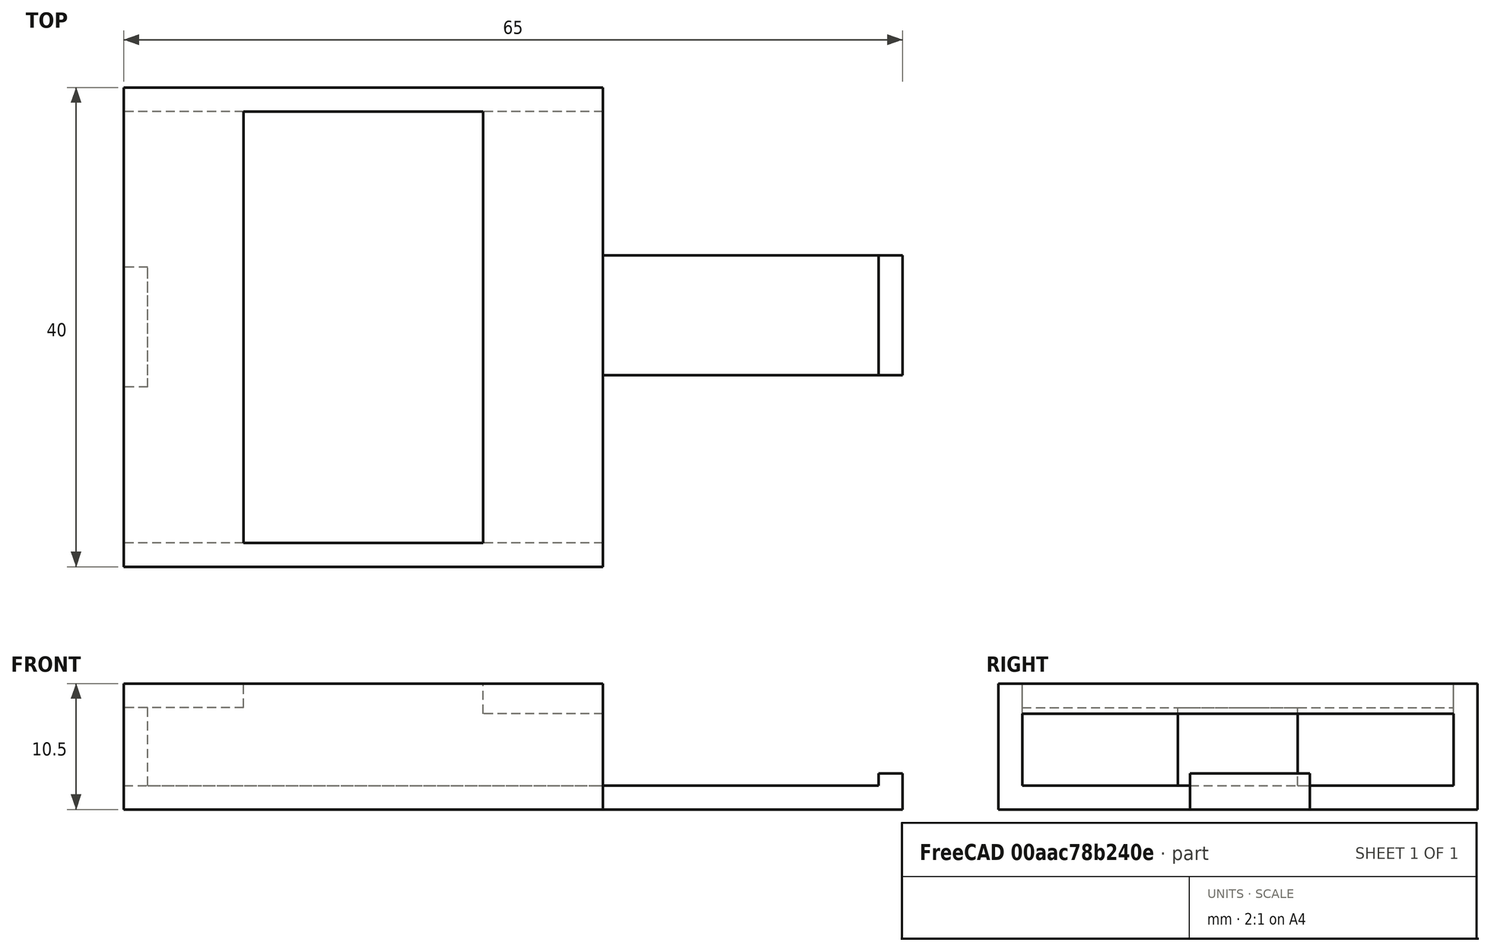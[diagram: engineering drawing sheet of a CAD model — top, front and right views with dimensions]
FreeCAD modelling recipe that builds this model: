
FCSTD DOCUMENT  (FreeCAD 0.20R29603 (Git))
Label: batteryholder
License: All rights reserved
LicenseURL: http://en.wikipedia.org/wiki/All_rights_reserved
objects: Part::Box×8, Part::MultiFuse×1
note: 9 computed .brp shape members not serialized (recipe doc carries the construction recipe); baked Part::Feature solids carry a one-line shape summary decoded from their .brp

FEATURE [Part::Box] Box  label="Cube"
  AttacherType = Attacher::AttachEngine3D
  Height = 2
  Length = 10
  Placement = pos=(0,-2,2.5) rot=(0,0,1;0rad)
  Width = 38
FEATURE [Part::Box] Box001  label="Cube001"
  AttacherType = Attacher::AttachEngine3D
  Height = 2
  Length = 40
  Placement = pos=(0,-1,-6) rot=(0,0,1;0rad)
  Width = 36
FEATURE [Part::Box] Box002  label="Cube002"
  AttacherType = Attacher::AttachEngine3D
  Height = 2.5
  Length = 10
  Placement = pos=(30,-2,2) rot=(0,0,1;0rad)
  Width = 38
FEATURE [Part::Box] Box003  label="Cube003"
  AttacherType = Attacher::AttachEngine3D
  Height = 10.5
  Length = 40
  Placement = pos=(0,-3,-6) rot=(0,0,1;0rad)
  Width = 2
FEATURE [Part::Box] Box004  label="Cube004"
  AttacherType = Attacher::AttachEngine3D
  Height = 10.5
  Length = 40
  Placement = pos=(0,35,-6) rot=(0,0,1;0rad)
  Width = 2
FEATURE [Part::Box] Box005  label="Cube005"
  AttacherType = Attacher::AttachEngine3D
  Height = 8.5
  Length = 2
  Placement = pos=(0,12,-4) rot=(0,0,1;0rad)
  Width = 10
FEATURE [Part::Box] Box006  label="Cube006"
  AttacherType = Attacher::AttachEngine3D
  Height = 2
  Length = 63
  Placement = pos=(2,13,-6) rot=(0,0,1;0rad)
  Width = 10
FEATURE [Part::Box] Box007  label="Cube007"
  AttacherType = Attacher::AttachEngine3D
  Height = 2
  Length = 2
  Placement = pos=(63,13,-5) rot=(0,0,1;0rad)
  Width = 10
FEATURE [Part::MultiFuse] Fusion
  Shapes = -> [Box,Box001,Box002,Box003,Box004,Box005,Box006,Box007]
